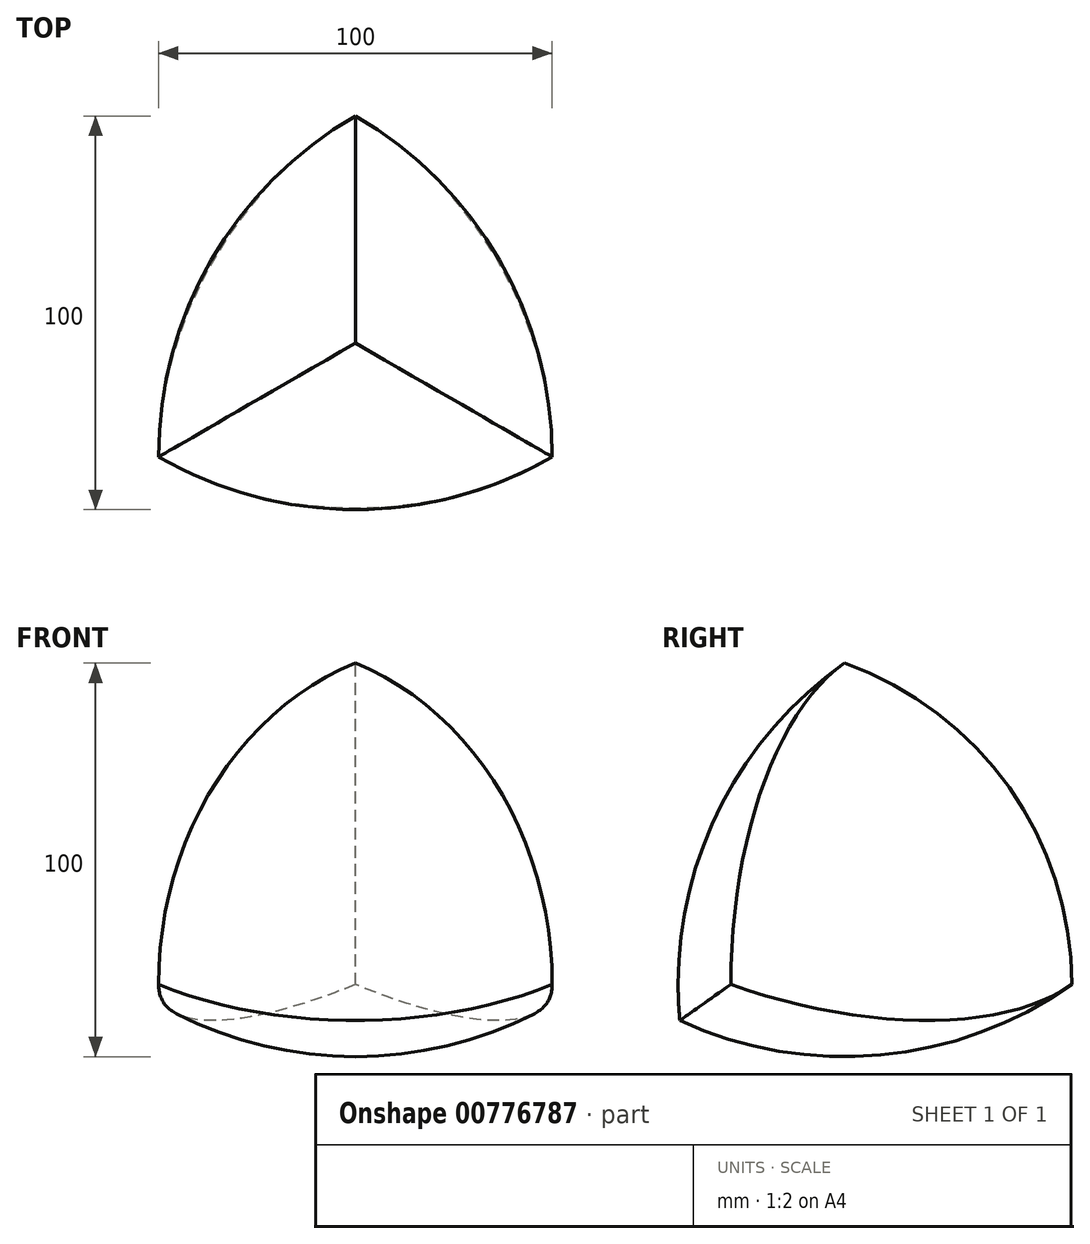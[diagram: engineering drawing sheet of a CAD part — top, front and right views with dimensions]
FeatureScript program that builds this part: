
annotation { "Feature Type Name" : "Feature", "Feature Type Description" : "" }
export const myFeature = defineFeature(function(context is Context, id is Id, definition is map)
    precondition{}
    {
        {
            var Q0;
            Q0=qCreatedBy(makeId("Top.planeOp"),FACE);
            var sketch = newSketch(context, id + "F0", { "sketchPlane" : qUnion([Q0])});
            skLineSegment(sketch, "E0", {"start": v(-50, -28.87) * mm, "end": v(0, 57.74) * mm, "construction": true});
            skLineSegment(sketch, "E1", {"start": v(0, 57.74) * mm, "end": v(50, -28.87) * mm, "construction": true});
            skLineSegment(sketch, "E2", {"start": v(50, -28.87) * mm, "end": v(-50, -28.87) * mm, "construction": true});
            skLineSegment(sketch, "E3", {"start": v(0, 57.74) * mm, "end": v(0, 0) * mm, "construction": true});
            skLineSegment(sketch, "E4", {"start": v(0, 0) * mm, "end": v(-50, -28.87) * mm, "construction": true});
            skLineSegment(sketch, "E5", {"start": v(0, 0) * mm, "end": v(50, -28.87) * mm, "construction": true});
            skArc(sketch, "E6", {"start": v(0, 157.74) * mm, "mid": v(-100, 57.74) * mm, "end": v(0, -42.26) * mm});
            skLineSegment(sketch, "E7", {"start": v(0, 157.74) * mm, "end": v(0, -42.26) * mm});
            skSolve(sketch);
        }
        {
            var Q0;
            Q0=qCreatedBy(makeId("Right.planeOp"),FACE);
            var sketch = newSketch(context, id + "F1", { "sketchPlane" : qUnion([Q0])});
            skLineSegment(sketch, "E8", {"start": v(-28.87, 0) * mm, "end": v(0, 81.65) * mm, "construction": true});
            skLineSegment(sketch, "E9", {"start": v(0, 81.65) * mm, "end": v(57.74, 0) * mm, "construction": true});
            skLineSegment(sketch, "E10", {"start": v(57.74, 0) * mm, "end": v(-28.87, 0) * mm, "construction": true});
            skSolve(sketch);
        }
        {
            var Q0;
            Q0=makeQuery(id+"F0.imprint","IMPRINT",FACE,{"disambiguationData":[TD([[makeQuery(id+"F0.imprint","IMPRINT",EDGE,{"derivedFrom":sQuery(id+"F0.wireOp",EDGE,"E6")}),1.0]])]});
            var Q1;
            Q1=sQuery(id+"F0.wireOp",EDGE,"E7");
            revolve(context, id + "F2", {"surfaceOperationType" : NewSurfaceOperationType.NEW, "entities" : qUnion([Q0]), "axis" : qUnion([Q1]), "revolveType" : RevolveType.FULL});
        }
        {
            var Q0;
            Q0=makeQuery(id+"F2.opRevolve","SWEPT_BODY",BODY,{"disambiguationData":[OSD([sQuery(id+"F0.wireOp",EDGE,"E6"),sQuery(id+"F0.wireOp",EDGE,"E7")])]});
            var Q1;
            Q1=sQuery(id+"F0.wireOp",EDGE,"E0");
            transform(context, id + "F3", {"entities" : qUnion([Q0]), "transformType" : TransformType.TRANSLATION_ENTITY, "oppositeDirectionEntity" : true, "transformLine" : qUnion([Q1]), "makeCopy" : true});
        }
        {
            var Q0;
            Q0=makeQuery(id+"F2.opRevolve","SWEPT_BODY",BODY,{"disambiguationData":[OSD([sQuery(id+"F0.wireOp",EDGE,"E6"),sQuery(id+"F0.wireOp",EDGE,"E7")])]});
            var Q1;
            Q1=sQuery(id+"F0.wireOp",EDGE,"E1");
            transform(context, id + "F4", {"entities" : qUnion([Q0]), "transformType" : TransformType.TRANSLATION_ENTITY, "oppositeDirectionEntity" : false, "transformLine" : qUnion([Q1]), "makeCopy" : true});
        }
        {
            var Q0;
            Q0=makeQuery(id+"F2.opRevolve","SWEPT_BODY",BODY,{"disambiguationData":[OSD([sQuery(id+"F0.wireOp",EDGE,"E6"),sQuery(id+"F0.wireOp",EDGE,"E7")])]});
            var Q1;
            Q1=sQuery(id+"F1.wireOp",EDGE,"E9");
            transform(context, id + "F5", {"entities" : qUnion([Q0]), "transformType" : TransformType.TRANSLATION_ENTITY, "oppositeDirectionEntity" : true, "transformLine" : qUnion([Q1]), "makeCopy" : true});
        }
        {
            var Q0;
            Q0=makeQuery(id+"F2.opRevolve","SWEPT_BODY",BODY,{"disambiguationData":[OSD([sQuery(id+"F0.wireOp",EDGE,"E6"),sQuery(id+"F0.wireOp",EDGE,"E7")])]});
            var Q1;
            Q1=makeQuery(id+"F3.opPattern","COPY",BODY,{"derivedFrom":makeQuery(id+"F2.opRevolve","SWEPT_BODY",BODY,{"disambiguationData":[OSD([sQuery(id+"F0.wireOp",EDGE,"E6"),sQuery(id+"F0.wireOp",EDGE,"E7")])]}),"instanceName":"1"});
            var Q2;
            Q2=makeQuery(id+"F4.opPattern","COPY",BODY,{"derivedFrom":makeQuery(id+"F2.opRevolve","SWEPT_BODY",BODY,{"disambiguationData":[OSD([sQuery(id+"F0.wireOp",EDGE,"E6"),sQuery(id+"F0.wireOp",EDGE,"E7")])]}),"instanceName":"1"});
            var Q3;
            Q3=makeQuery(id+"F5.opPattern","COPY",BODY,{"derivedFrom":makeQuery(id+"F2.opRevolve","SWEPT_BODY",BODY,{"disambiguationData":[OSD([sQuery(id+"F0.wireOp",EDGE,"E6"),sQuery(id+"F0.wireOp",EDGE,"E7")])]}),"instanceName":"1"});
            booleanBodies(context, id + "F6", {"operationType" : BooleanOperationType.INTERSECTION, "tools" : qUnion([Q0, Q1, Q2, Q3])});
        }
    });
